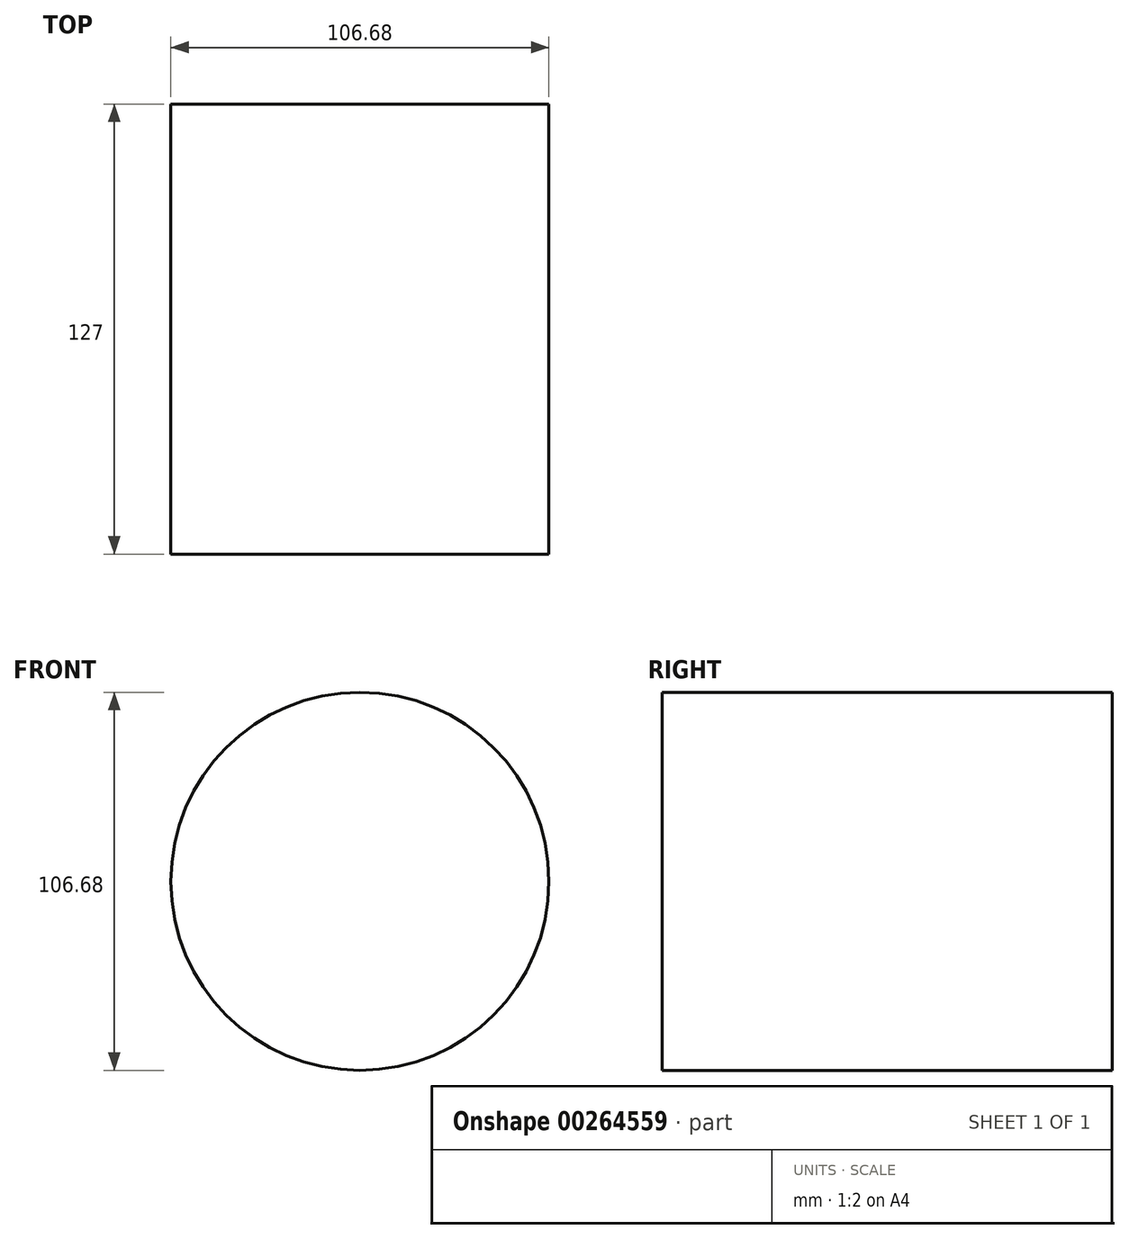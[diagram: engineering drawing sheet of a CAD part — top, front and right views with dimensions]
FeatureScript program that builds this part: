
annotation { "Feature Type Name" : "Feature", "Feature Type Description" : "" }
export const myFeature = defineFeature(function(context is Context, id is Id, definition is map)
    precondition{}
    {
        {
            var Q0;
            Q0=qCreatedBy(makeId("Front.planeOp"),FACE);
            var sketch = newSketch(context, id + "F0", { "sketchPlane" : qUnion([Q0])});
            skCircle(sketch, "E0", {"center": v(0, 0) * mm, "radius": 53.34 * mm});
            skSolve(sketch);
        }
        {
            var Q0;
            Q0 = qSketchRegion(id + "F0", true);
            extrude(context, id + "F1", {"entities" : qUnion([Q0]), "depth" : 127 * mm});
        }
    });
